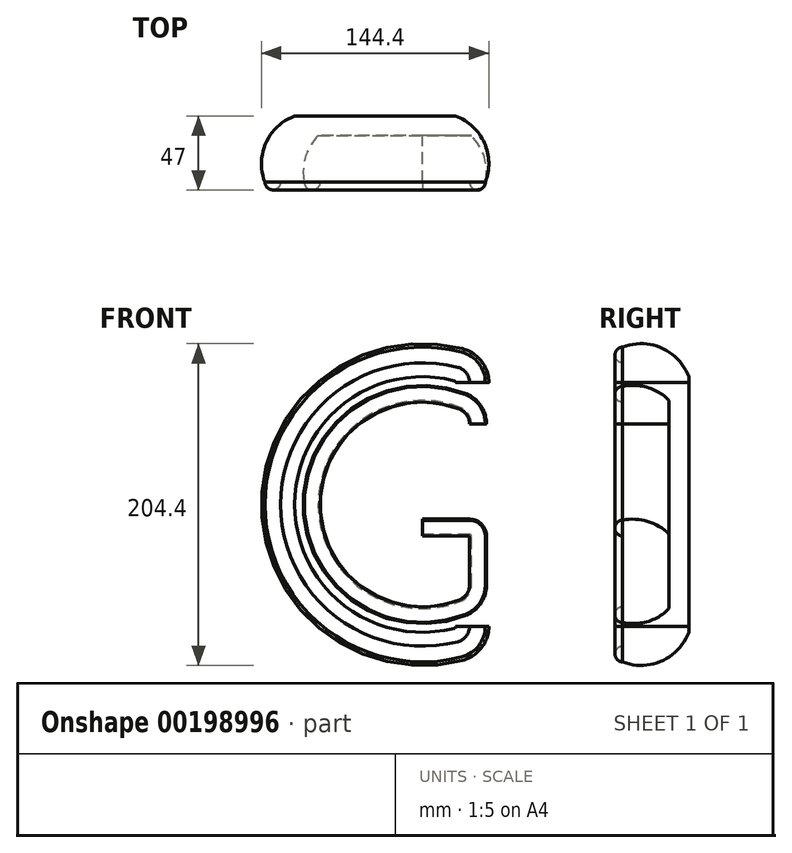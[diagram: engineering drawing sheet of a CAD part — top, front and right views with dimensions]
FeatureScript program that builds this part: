
annotation { "Feature Type Name" : "Feature", "Feature Type Description" : "" }
export const myFeature = defineFeature(function(context is Context, id is Id, definition is map)
    precondition{}
    {
        {
            var Q0;
            Q0=qCreatedBy(makeId("Front.planeOp"),FACE);
            var sketch = newSketch(context, id + "F0", { "sketchPlane" : qUnion([Q0])});
            skArc(sketch, "E0", {"start": v(25, 96.82) * mm, "mid": v(-100, 0) * mm, "end": v(25, -96.82) * mm});
            skArc(sketch, "E1", {"start": v(27.27, 69.87) * mm, "mid": v(-75, 0) * mm, "end": v(27.27, -69.87) * mm});
            skLineSegment(sketch, "E2", {"start": v(40, -20) * mm, "end": v(40, -51.23) * mm});
            skPoint(sketch, "E3.visualSharp", {"position": v(40, 91.65) * mm});
            skArc(sketch, "E3.filletArc", {"start": v(40, 77.46) * mm, "mid": v(35.81, 89.7) * mm, "end": v(25, 96.82) * mm});
            skPoint(sketch, "E4.visualSharp", {"position": v(40, -91.65) * mm});
            skArc(sketch, "E4.filletArc", {"start": v(25, -96.82) * mm, "mid": v(35.81, -89.7) * mm, "end": v(40, -77.46) * mm});
            skArc(sketch, "E5.filletArc", {"start": v(40, 51.23) * mm, "mid": v(36.51, 62.52) * mm, "end": v(27.27, 69.87) * mm});
            skArc(sketch, "E6.filletArc", {"start": v(27.27, -69.87) * mm, "mid": v(36.51, -62.52) * mm, "end": v(40, -51.23) * mm});
            skLineSegment(sketch, "E7", {"start": v(30, -10) * mm, "end": v(0, -10) * mm});
            skArc(sketch, "E8.filletArc", {"start": v(40, -20) * mm, "mid": v(37.07, -12.93) * mm, "end": v(30, -10) * mm});
            skSolve(sketch);
        }
        {
            var Q0;
            Q0=sQuery(id+"F0.wireOp",VERTEX,"E3.filletArc.start");
            var Q1;
            Q1=sQuery(id+"F0.wireOp",EDGE,"E3.filletArc");
            cPlane(context, id + "F1", {"entities" : qUnion([Q0, Q1]), "cplaneType" : CPlaneType.CURVE_POINT, "offset" : 25 * mm, "width" : 150 * mm, "height" : 150 * mm});
        }
        {
            var Q0;
            Q0=qCreatedBy(id+"F1.planeOp",FACE);
            var sketch = newSketch(context, id + "F2", { "sketchPlane" : qUnion([Q0])});
            skArc(sketch, "E9", {"start": v(30, 0) * mm, "mid": v(35, -4.87) * mm, "end": v(40, 0) * mm});
            skArc(sketch, "E10", {"start": v(40, 0) * mm, "mid": v(39.37, 24.92) * mm, "end": v(21.16, 41.96) * mm});
            skSolve(sketch);
        }
        {
            var Q0;
            Q0 = qSketchRegion(id + "F2", true);
            var Q1;
            Q1=sQuery(id+"F2.wireOp",EDGE,"E9");
            var Q2;
            Q2=sQuery(id+"F2.wireOp",EDGE,"E10");
            var Q3;
            Q3=sQuery(id+"F0.wireOp",EDGE,"E3.filletArc");
            var Q4;
            Q4=sQuery(id+"F0.wireOp",EDGE,"E0");
            var Q5;
            Q5=sQuery(id+"F0.wireOp",EDGE,"E4.filletArc");
            sweep(context, id + "F3", {"bodyType" : ToolBodyType.SURFACE, "profiles" : qUnion([Q0]), "surfaceProfiles" : qUnion([Q1, Q2]), "path" : qUnion([Q3, Q4, Q5])});
        }
        {
            var Q0;
            Q0=sQuery(id+"F0.wireOp",EDGE,"E5.filletArc");
            var Q1;
            Q1=sQuery(id+"F0.wireOp",VERTEX,"E5.filletArc.start");
            cPlane(context, id + "F4", {"entities" : qUnion([Q0, Q1]), "cplaneType" : CPlaneType.CURVE_POINT, "offset" : 25 * mm, "width" : 150 * mm, "height" : 150 * mm});
        }
        {
            var Q0;
            Q0=qCreatedBy(id+"F4.planeOp",FACE);
            var sketch = newSketch(context, id + "F5", { "sketchPlane" : qUnion([Q0])});
            skArc(sketch, "E11", {"start": v(30, 0) * mm, "mid": v(35, -5.04) * mm, "end": v(40, 0) * mm});
            skArc(sketch, "E12", {"start": v(40, 0) * mm, "mid": v(39.32, 15.89) * mm, "end": v(31.14, 29.52) * mm});
            skSolve(sketch);
        }
        {
            var Q0;
            Q0 = qSketchRegion(id + "F5", true);
            var Q1;
            Q1=sQuery(id+"F5.wireOp",EDGE,"E11");
            var Q2;
            Q2=sQuery(id+"F5.wireOp",EDGE,"E12");
            var Q3;
            Q3=sQuery(id+"F0.wireOp",EDGE,"E5.filletArc");
            var Q4;
            Q4=sQuery(id+"F0.wireOp",EDGE,"E1");
            var Q5;
            Q5=sQuery(id+"F0.wireOp",EDGE,"E6.filletArc");
            var Q6;
            Q6=sQuery(id+"F0.wireOp",EDGE,"E2");
            var Q7;
            Q7=sQuery(id+"F0.wireOp",EDGE,"E8.filletArc");
            var Q8;
            Q8=sQuery(id+"F0.wireOp",EDGE,"E7");
            sweep(context, id + "F6", {"bodyType" : ToolBodyType.SURFACE, "profiles" : qUnion([Q0]), "surfaceProfiles" : qUnion([Q1, Q2]), "path" : qUnion([Q3, Q4, Q5, Q6, Q7, Q8])});
        }
    });
